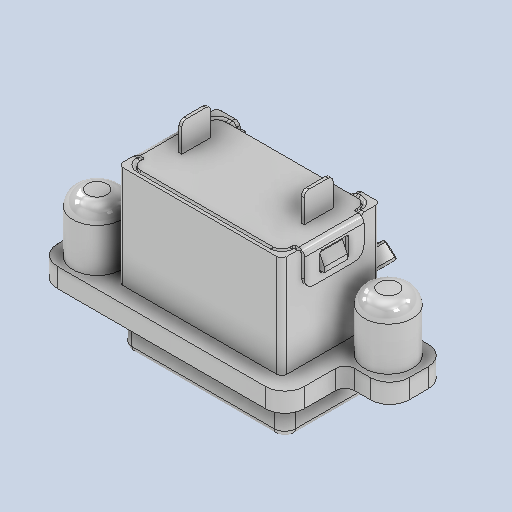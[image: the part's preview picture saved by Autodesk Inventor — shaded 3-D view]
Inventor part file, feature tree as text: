
AUTODESK INVENTOR PART (.ipt)
format: ipt  version: 2024.2 (Build 282272000, 272)  size: 1,376,256 bytes
history: native  units: mm
features: extrude x3, plane x1, fillet x1, imported_body x1
ambient origin geometry x8: Origin, YZ Plane, XZ Plane, XY Plane, X Axis, Y Axis, Z Axis, Center Point
bodies: Solid1 (feature_tree)
feature tree (6):
  extrude  "Extrusion1"  TaperAngle=0.0deg  [1 undecoded]
  extrude  "Extrusion2"  TaperAngle=0.0deg  [1 undecoded]
  plane  "Work Plane1"
  extrude  "Extrusion3"  Depth=4.4mm
  fillet  "Fillet1"  Radius=6.35mm
  imported_body  "Imported2"
note: 2 required parameter values undecoded (feature->parameter linkage not recoverable at this tier; creation-order binding heuristic only, values carry confidence <= 0.55)
